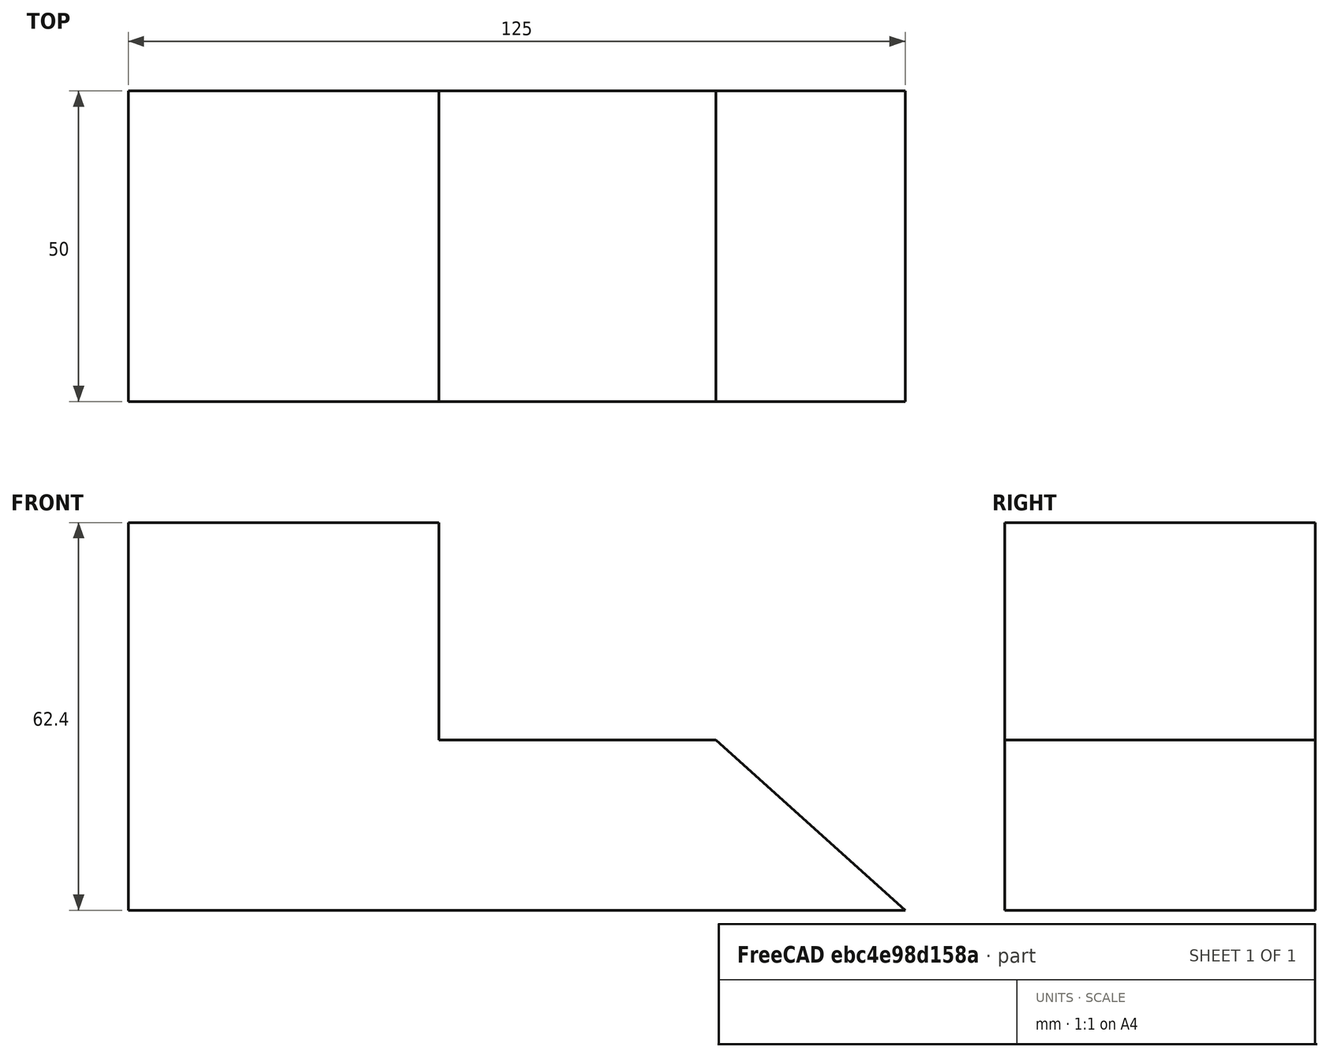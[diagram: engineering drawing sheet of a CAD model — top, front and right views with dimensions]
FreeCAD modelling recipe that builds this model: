
FCSTD DOCUMENT  (FreeCAD 0.21R33771 (Git))
Label: pieza-01
License: All rights reserved
LicenseURL: http://en.wikipedia.org/wiki/All_rights_reserved
objects: Sketcher::SketchObject×1, PartDesign::Pad×1, PartDesign::Body×1
note: 4 computed .brp shape members not serialized (recipe doc carries the construction recipe); baked Part::Feature solids carry a one-line shape summary decoded from their .brp

FEATURE [Sketcher::SketchObject] Sketch
  FullyConstrained = true
  MapMode = 5
  Placement = pos=(0,0,0) rot=(1,0,0;1.5708rad)
  Support = -> [XZ_Plane]
  sketch-geometry (6):
    g0: LineSegment StartX=0 StartY=62.4 StartZ=0 EndX=50 EndY=62.4 EndZ=0
    g1: LineSegment StartX=50 StartY=62.4 StartZ=0 EndX=50 EndY=27.4 EndZ=0
    g2: LineSegment StartX=50 StartY=27.4 StartZ=0 EndX=94.5692 EndY=27.4 EndZ=0
    g3: LineSegment StartX=94.5692 StartY=27.4 StartZ=0 EndX=125 EndY=0 EndZ=0
    g4: LineSegment StartX=125 StartY=0 StartZ=0 EndX=0 EndY=0 EndZ=0
    g5: LineSegment StartX=0 StartY=0 StartZ=0 EndX=0 EndY=62.4 EndZ=0
  constraints (17):
    c: Horizontal(g0)
    c: Coincident(g0,g1)
    c: Vertical(g1)
    c: Coincident(g1,g2)
    c: Horizontal(g2)
    c: Coincident(g2,g3)
    c: Coincident(g3,g4)
    c: Coincident(g4,g-1)
    c: Horizontal(g4)
    c: Coincident(g4,g5)
    c: Coincident(g5,g0)
    c: Vertical(g5)
    c: DistanceX(g4,g4) = 125  'Base'
    c: DistanceY(g5,g5) = 62.4
    c: DistanceX(g0,g0) = 50
    c: DistanceY(g3,g2) = 27.4
    c: Angle(g3,g4) = 0.733038
FEATURE [PartDesign::Pad] Pad
  Direction = (0,-1,2e-16)
  Length = 50
  Length2 = 10
  Placement = pos=(0,0,0) rot=(1,0,0;1.5708rad)
  Profile = -> Sketch
  ReferenceAxis = -> Sketch [N_Axis]
  Refine = true
  Type = 0
FEATURE [PartDesign::Body] Body
  Group = -> [Sketch,Pad]
  Origin = -> Origin
  Tip = -> Pad
